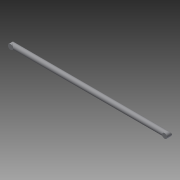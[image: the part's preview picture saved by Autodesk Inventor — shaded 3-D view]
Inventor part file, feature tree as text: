
AUTODESK INVENTOR PART (.ipt)
format: ipt  version: 2013 (Build 170138000, 138)  size: 71,680 bytes
history: native  units: in
note: dims shown in document units (in); Inventor stores cm internally (conversion verified against a paired STEP export)
features: sketch x2, sweep x1
ambient origin geometry x8: Origin, YZ Plane, XZ Plane, XY Plane, X Axis, Y Axis, Z Axis, Center Point
bodies: Solid1 (feature_tree)
feature tree (3):
  sweep  "Sweep1"
  sketch  "Sketch1"  dims[d1=0.5in d2=0.0in]
  sketch  "Sketch2"  dims[d3=0.25in d4=15.5in]
